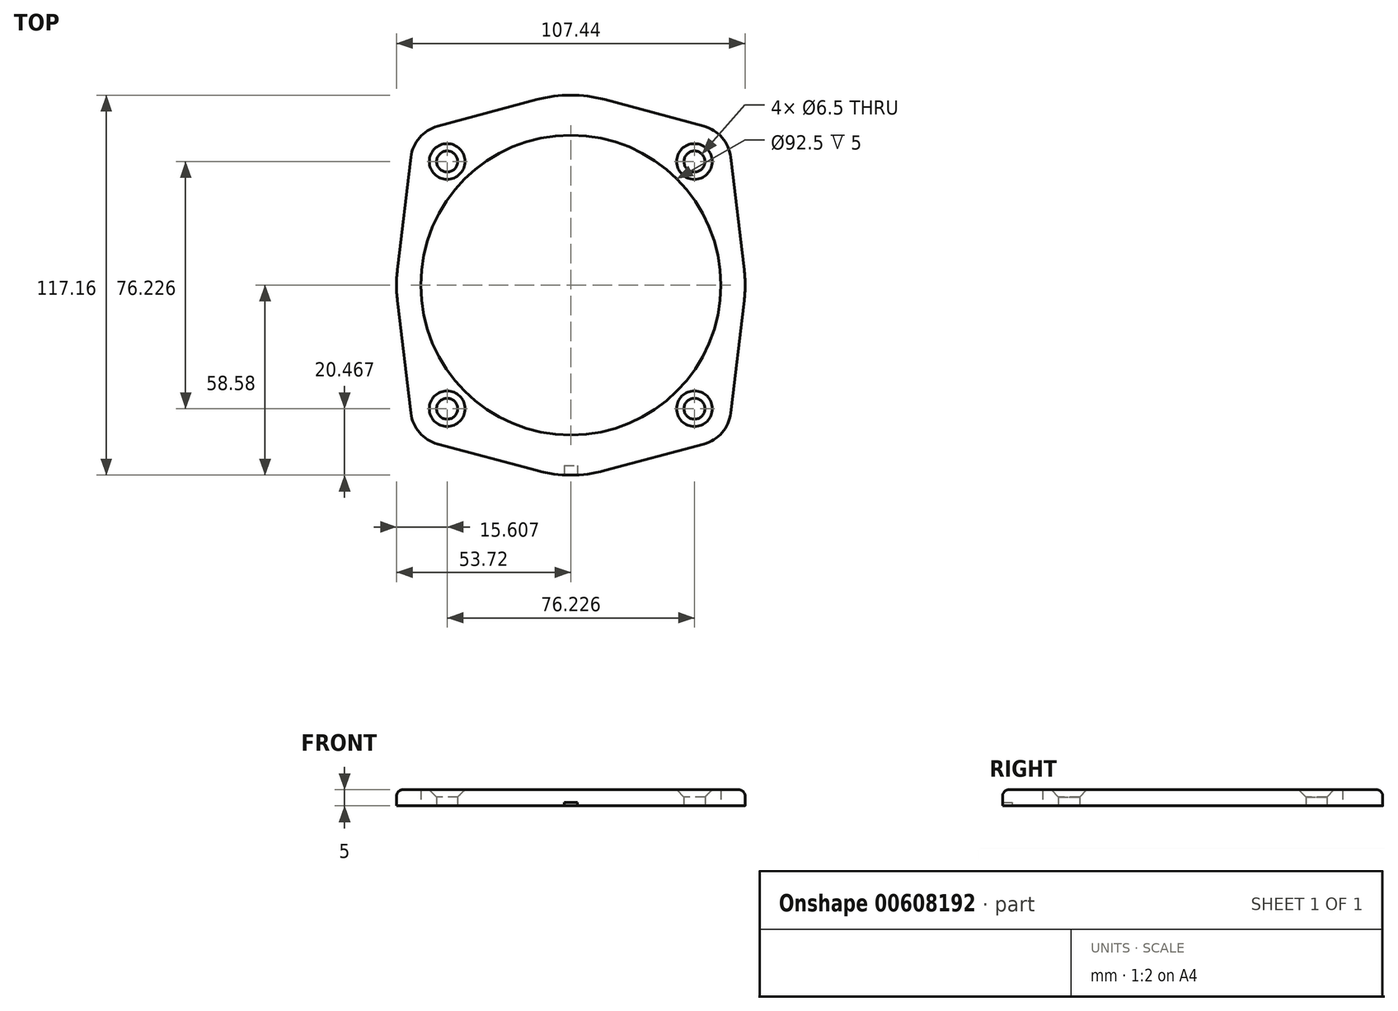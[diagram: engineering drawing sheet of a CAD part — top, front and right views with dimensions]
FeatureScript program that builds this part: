
annotation { "Feature Type Name" : "Feature", "Feature Type Description" : "" }
export const myFeature = defineFeature(function(context is Context, id is Id, definition is map)
    precondition{}
    {
        {
            var Q0;
            Q0=qCreatedBy(makeId("Top.planeOp"),FACE);
            var sketch = newSketch(context, id + "F0", { "sketchPlane" : qUnion([Q0])});
            skCircle(sketch, "E0", {"center": v(0, 0) * mm, "radius": 46.25 * mm});
            skCircle(sketch, "E1", {"center": v(38.11, 38.11) * mm, "radius": 3.25 * mm});
            skLineSegment(sketch, "E2", {"start": v(0, 0) * mm, "end": v(38.11, 38.11) * mm, "construction": true});
            skCircle(sketch, "E3.1.0", {"center": v(-38.11, 38.11) * mm, "radius": 3.25 * mm});
            skCircle(sketch, "E3.2.0", {"center": v(-38.11, -38.11) * mm, "radius": 3.25 * mm});
            skCircle(sketch, "E4.1.3.0", {"center": v(38.11, -38.11) * mm, "radius": 3.25 * mm});
            skPoint(sketch, "E5", {"position": v(0, 60) * mm});
            skPoint(sketch, "E6", {"position": v(54, 0) * mm});
            skPoint(sketch, "E7", {"position": v(0, -60) * mm});
            skPoint(sketch, "E8", {"position": v(-54, 0) * mm});
            skLineSegment(sketch, "E9", {"start": v(-53.43, 4.75) * mm, "end": v(-49.28, 39.45) * mm});
            skLineSegment(sketch, "E10", {"start": v(-53.43, -4.75) * mm, "end": v(-49.28, -39.45) * mm});
            skLineSegment(sketch, "E11", {"start": v(53.43, 4.75) * mm, "end": v(49.28, 39.45) * mm});
            skLineSegment(sketch, "E12", {"start": v(53.43, -4.75) * mm, "end": v(49.28, -39.45) * mm});
            skLineSegment(sketch, "E13", {"start": v(-10.38, 57.21) * mm, "end": v(-41.03, 48.98) * mm});
            skLineSegment(sketch, "E14", {"start": v(10.38, 57.21) * mm, "end": v(41.03, 48.98) * mm});
            skLineSegment(sketch, "E15", {"start": v(10.38, -57.21) * mm, "end": v(41.03, -48.98) * mm});
            skLineSegment(sketch, "E16", {"start": v(-10.38, -57.21) * mm, "end": v(-41.03, -48.98) * mm});
            skLineSegment(sketch, "E17", {"start": v(0, 0) * mm, "end": v(0, 60) * mm, "construction": true});
            skLineSegment(sketch, "E18", {"start": v(0, 0) * mm, "end": v(0, -60) * mm, "construction": true});
            skLineSegment(sketch, "E19", {"start": v(0, 0) * mm, "end": v(54, 0) * mm, "construction": true});
            skLineSegment(sketch, "E20", {"start": v(0, 0) * mm, "end": v(-54, 0) * mm, "construction": true});
            skArc(sketch, "E21.filletArc", {"start": v(10.38, 57.21) * mm, "mid": v(0, 58.58) * mm, "end": v(-10.38, 57.21) * mm});
            skArc(sketch, "E22.filletArc", {"start": v(-10.38, -57.21) * mm, "mid": v(0, -58.58) * mm, "end": v(10.38, -57.21) * mm});
            skArc(sketch, "E23.filletArc", {"start": v(-53.43, 4.75) * mm, "mid": v(-53.72, 0) * mm, "end": v(-53.43, -4.75) * mm});
            skArc(sketch, "E24.filletArc", {"start": v(53.43, -4.75) * mm, "mid": v(53.72, 0) * mm, "end": v(53.43, 4.75) * mm});
            skLineSegment(sketch, "E25", {"start": v(-41.03, 48.98) * mm, "end": v(-41.03, 48.98) * mm});
            skLineSegment(sketch, "E26", {"start": v(-49.28, 39.45) * mm, "end": v(-49.28, 39.45) * mm});
            skLineSegment(sketch, "E27", {"start": v(49.28, 39.45) * mm, "end": v(49.28, 39.45) * mm});
            skArc(sketch, "E28", {"start": v(41.03, 48.98) * mm, "mid": v(29.6, 30.75) * mm, "end": v(49.28, 39.45) * mm, "construction": true});
            skArc(sketch, "E29", {"start": v(49.28, 39.45) * mm, "mid": v(46.62, 45.48) * mm, "end": v(41.03, 48.98) * mm});
            skArc(sketch, "E30", {"start": v(49.28, -39.45) * mm, "mid": v(29.6, -30.75) * mm, "end": v(41.03, -48.98) * mm, "construction": true});
            skArc(sketch, "E31", {"start": v(41.03, -48.98) * mm, "mid": v(46.62, -45.48) * mm, "end": v(49.28, -39.45) * mm});
            skLineSegment(sketch, "E32", {"start": v(-41.03, -48.98) * mm, "end": v(-41.03, -48.98) * mm});
            skArc(sketch, "E33", {"start": v(-49.28, 39.45) * mm, "mid": v(-29.6, 30.75) * mm, "end": v(-41.03, 48.98) * mm, "construction": true});
            skArc(sketch, "E34", {"start": v(-41.03, 48.98) * mm, "mid": v(-46.62, 45.48) * mm, "end": v(-49.28, 39.45) * mm});
            skArc(sketch, "E35", {"start": v(-49.28, -39.45) * mm, "mid": v(-46.62, -45.48) * mm, "end": v(-41.03, -48.98) * mm});
            skArc(sketch, "E36", {"start": v(-41.03, -48.98) * mm, "mid": v(-35.04, -27.3) * mm, "end": v(-41.35, -48.89) * mm});
            skArc(sketch, "E37", {"start": v(-41.35, -48.89) * mm, "mid": v(-29.5, -30.87) * mm, "end": v(-49.28, -39.45) * mm, "construction": true});
            skLineSegment(sketch, "E38", {"start": v(-49.28, -39.45) * mm, "end": v(-49.28, -39.45) * mm});
            skSolve(sketch);
        }
        {
            var Q0;
            Q0 = qSketchRegion(id + "F0", true);
            extrude(context, id + "F1", {"entities" : qUnion([Q0]), "depth" : 5 * mm, "offsetDistance" : 25 * mm});
        }
        {
            var Q0;
            Q0=makeQuery(id+"F1.opExtrude","CAP_EDGE",EDGE,{"disambiguationData":[OSD([sQuery(id+"F0.wireOp",EDGE,"E13")])],"isStart":false});
            fillet(context, id + "F2", {"entities" : qUnion([Q0]), "radius" : 2 * mm, "tangentPropagation" : true, "allowEdgeOverflow" : false});
        }
        {
            var Q0;
            Q0=makeQuery(id+"F1.opExtrude","CAP_EDGE",EDGE,{"disambiguationData":[OSD([sQuery(id+"F0.wireOp",EDGE,"E3.1.0")])],"isStart":false});
            var Q1;
            Q1=makeQuery(id+"F1.opExtrude","CAP_EDGE",EDGE,{"disambiguationData":[OSD([sQuery(id+"F0.wireOp",EDGE,"E1")])],"isStart":false});
            var Q2;
            Q2=makeQuery(id+"F1.opExtrude","CAP_EDGE",EDGE,{"disambiguationData":[OSD([sQuery(id+"F0.wireOp",EDGE,"E4.1.3.0")])],"isStart":false});
            var Q3;
            Q3=makeQuery(id+"F1.opExtrude","CAP_EDGE",EDGE,{"disambiguationData":[OSD([sQuery(id+"F0.wireOp",EDGE,"E3.2.0")])],"isStart":false});
            chamfer(context, id + "F3", {"entities" : qUnion([Q0, Q1, Q2, Q3]), "width" : 2.25 * mm, "tangentPropagation" : true});
        }
        {
            var Q0;
            Q0=qCreatedBy(makeId("Right.planeOp"),FACE);
            var sketch = newSketch(context, id + "F4", { "sketchPlane" : qUnion([Q0])});
            skLineSegment(sketch, "E39.0", {"start": v(-57.21, 0) * mm, "end": v(-58.58, 0) * mm});
            skLineSegment(sketch, "E39.1", {"start": v(-57.21, 0) * mm, "end": v(-48.98, 0) * mm});
            skLineSegment(sketch, "E40", {"start": v(-58.58, 0) * mm, "end": v(-58.58, 1) * mm});
            skLineSegment(sketch, "E41", {"start": v(-58.58, 1) * mm, "end": v(-55.58, 1) * mm});
            skLineSegment(sketch, "E42", {"start": v(-55.58, 1) * mm, "end": v(-55.58, 0) * mm});
            skSolve(sketch);
        }
        {
            var Q0;
            Q0 = qSketchRegion(id + "F4", true);
            extrude(context, id + "F5", {"entities" : qUnion([Q0]), "operationType" : NewBodyOperationType.REMOVE, "oppositeDirection" : true, "depth" : 2 * mm, "offsetDistance" : 25 * mm, "hasSecondDirection" : true, "secondDirectionOppositeDirection" : false, "secondDirectionDepth" : 2 * mm});
        }
    });
